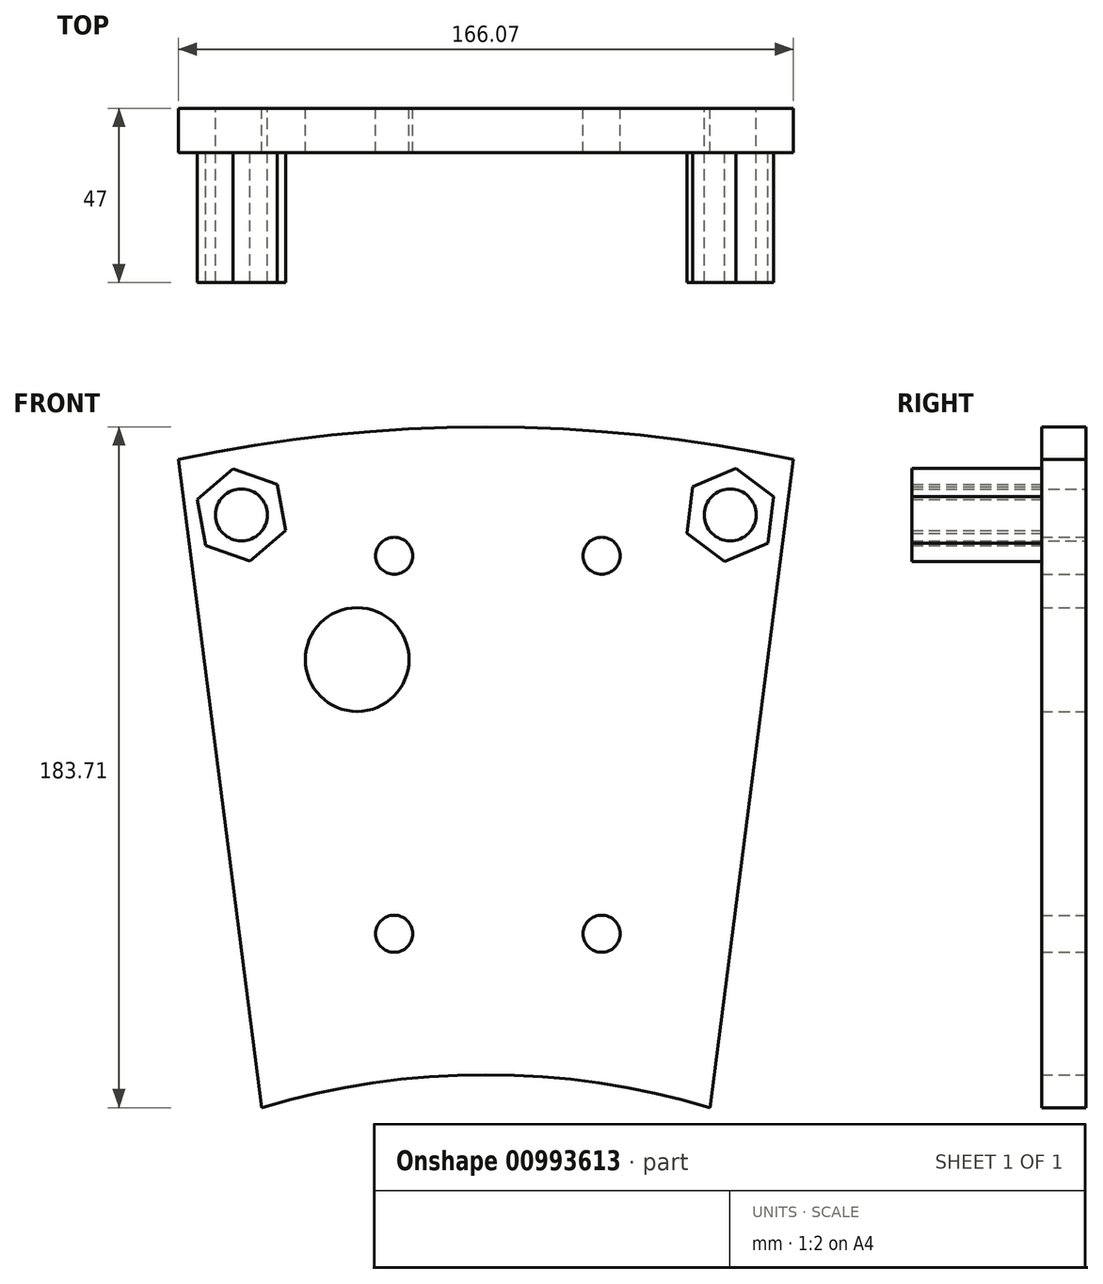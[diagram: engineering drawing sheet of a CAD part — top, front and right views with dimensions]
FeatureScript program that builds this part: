
annotation { "Feature Type Name" : "Feature", "Feature Type Description" : "" }
export const myFeature = defineFeature(function(context is Context, id is Id, definition is map)
    precondition{}
    {
        {
            var Q0;
            Q0=qCreatedBy(makeId("Front.planeOp"),FACE);
            var sketch = newSketch(context, id + "F0", { "sketchPlane" : qUnion([Q0])});
            skLineSegment(sketch, "E0", {"start": v(-73.8, 68.94) * mm, "end": v(-51.26, -106.06) * mm});
            skArc(sketch, "E1", {"start": v(69.74, -106.06) * mm, "mid": v(9.24, -97.16) * mm, "end": v(-51.26, -106.06) * mm});
            skArc(sketch, "E2", {"start": v(92.28, 68.94) * mm, "mid": v(9.24, 77.65) * mm, "end": v(-73.8, 68.94) * mm});
            skLineSegment(sketch, "E3", {"start": v(69.74, -106.06) * mm, "end": v(92.28, 68.94) * mm});
            skCircle(sketch, "E4", {"center": v(-15.5, 42.88) * mm, "radius": 5 * mm});
            skCircle(sketch, "E5", {"center": v(40.5, 42.88) * mm, "radius": 5 * mm});
            skCircle(sketch, "E6", {"center": v(-15.5, -59.12) * mm, "radius": 5 * mm});
            skCircle(sketch, "E7", {"center": v(40.5, -59.12) * mm, "radius": 5 * mm});
            skCircle(sketch, "E8", {"center": v(-25.5, 14.88) * mm, "radius": 14 * mm});
            skCircle(sketch, "E9", {"center": v(-56.73, 53.91) * mm, "radius": 7 * mm});
            skCircle(sketch, "E10", {"center": v(75.22, 53.91) * mm, "radius": 7 * mm});
            skSolve(sketch);
        }
        {
            var Q0;
            Q0=makeQuery(id+"F0.imprint","IMPRINT",FACE,{"disambiguationData":[TD([[makeQuery(id+"F0.imprint","IMPRINT",EDGE,{"derivedFrom":sQuery(id+"F0.wireOp",EDGE,"E0")}),1.0]])]});
            extrude(context, id + "F1", {"entities" : qUnion([Q0]), "depth" : 12 * mm, "offsetDistance" : 25 * mm});
        }
        {
            var Q0;
            Q0=makeQuery(id+"F1.opExtrude","CAP_FACE",FACE,{"disambiguationData":[OSD([sQuery(id+"F0.wireOp",EDGE,"E0"),sQuery(id+"F0.wireOp",EDGE,"E1"),sQuery(id+"F0.wireOp",EDGE,"E2"),sQuery(id+"F0.wireOp",EDGE,"E3"),sQuery(id+"F0.wireOp",EDGE,"E4"),sQuery(id+"F0.wireOp",EDGE,"E5"),sQuery(id+"F0.wireOp",EDGE,"E6"),sQuery(id+"F0.wireOp",EDGE,"E7"),sQuery(id+"F0.wireOp",EDGE,"E8"),sQuery(id+"F0.wireOp",EDGE,"E9"),sQuery(id+"F0.wireOp",EDGE,"E10")])],"isStart":false});
            var sketch = newSketch(context, id + "F2", { "sketchPlane" : qUnion([Q0])});
            skCircle(sketch, "E11.cCircle", {"center": v(-56.73, 53.91) * mm, "radius": 12.7 * mm, "construction": true});
            skLineSegment(sketch, "E11.0", {"start": v(-47.08, 62.17) * mm, "end": v(-44.76, 49.68) * mm});
            skLineSegment(sketch, "E11.1", {"start": v(-44.76, 49.68) * mm, "end": v(-54.42, 41.43) * mm});
            skLineSegment(sketch, "E11.2", {"start": v(-54.42, 41.43) * mm, "end": v(-66.39, 45.66) * mm});
            skLineSegment(sketch, "E11.3", {"start": v(-66.39, 45.66) * mm, "end": v(-68.7, 58.15) * mm});
            skLineSegment(sketch, "E11.4", {"start": v(-68.7, 58.15) * mm, "end": v(-59.05, 66.4) * mm});
            skLineSegment(sketch, "E11.5", {"start": v(-59.05, 66.4) * mm, "end": v(-47.08, 62.17) * mm});
            skCircle(sketch, "E12.cCircle", {"center": v(75.22, 53.91) * mm, "radius": 12.7 * mm, "construction": true});
            skLineSegment(sketch, "E12.0", {"start": v(65.05, 61.53) * mm, "end": v(76.73, 66.53) * mm});
            skLineSegment(sketch, "E12.1", {"start": v(76.73, 66.53) * mm, "end": v(86.9, 58.91) * mm});
            skLineSegment(sketch, "E12.2", {"start": v(86.9, 58.91) * mm, "end": v(85.4, 46.3) * mm});
            skLineSegment(sketch, "E12.3", {"start": v(85.4, 46.3) * mm, "end": v(73.71, 41.3) * mm});
            skLineSegment(sketch, "E12.4", {"start": v(73.71, 41.3) * mm, "end": v(63.55, 48.91) * mm});
            skLineSegment(sketch, "E12.5", {"start": v(63.55, 48.91) * mm, "end": v(65.05, 61.53) * mm});
            skCircle(sketch, "E13", {"center": v(-56.73, 53.91) * mm, "radius": 7 * mm});
            skCircle(sketch, "E14", {"center": v(75.22, 53.91) * mm, "radius": 7 * mm});
            skSolve(sketch);
        }
        {
            var Q0;
            Q0=makeQuery(id+"F2.imprint","IMPRINT",FACE,{"disambiguationData":[TD([[makeQuery(id+"F2.imprint","IMPRINT",EDGE,{"derivedFrom":sQuery(id+"F2.wireOp",EDGE,"E11.0")}),-1.0]])]});
            var Q1;
            Q1=makeQuery(id+"F2.imprint","IMPRINT",FACE,{"disambiguationData":[TD([[makeQuery(id+"F2.imprint","IMPRINT",EDGE,{"derivedFrom":sQuery(id+"F2.wireOp",EDGE,"E12.0")}),-1.0]])]});
            extrude(context, id + "F3", {"entities" : qUnion([Q0, Q1]), "operationType" : NewBodyOperationType.ADD, "depth" : 35 * mm, "offsetDistance" : 25 * mm});
        }
    });
